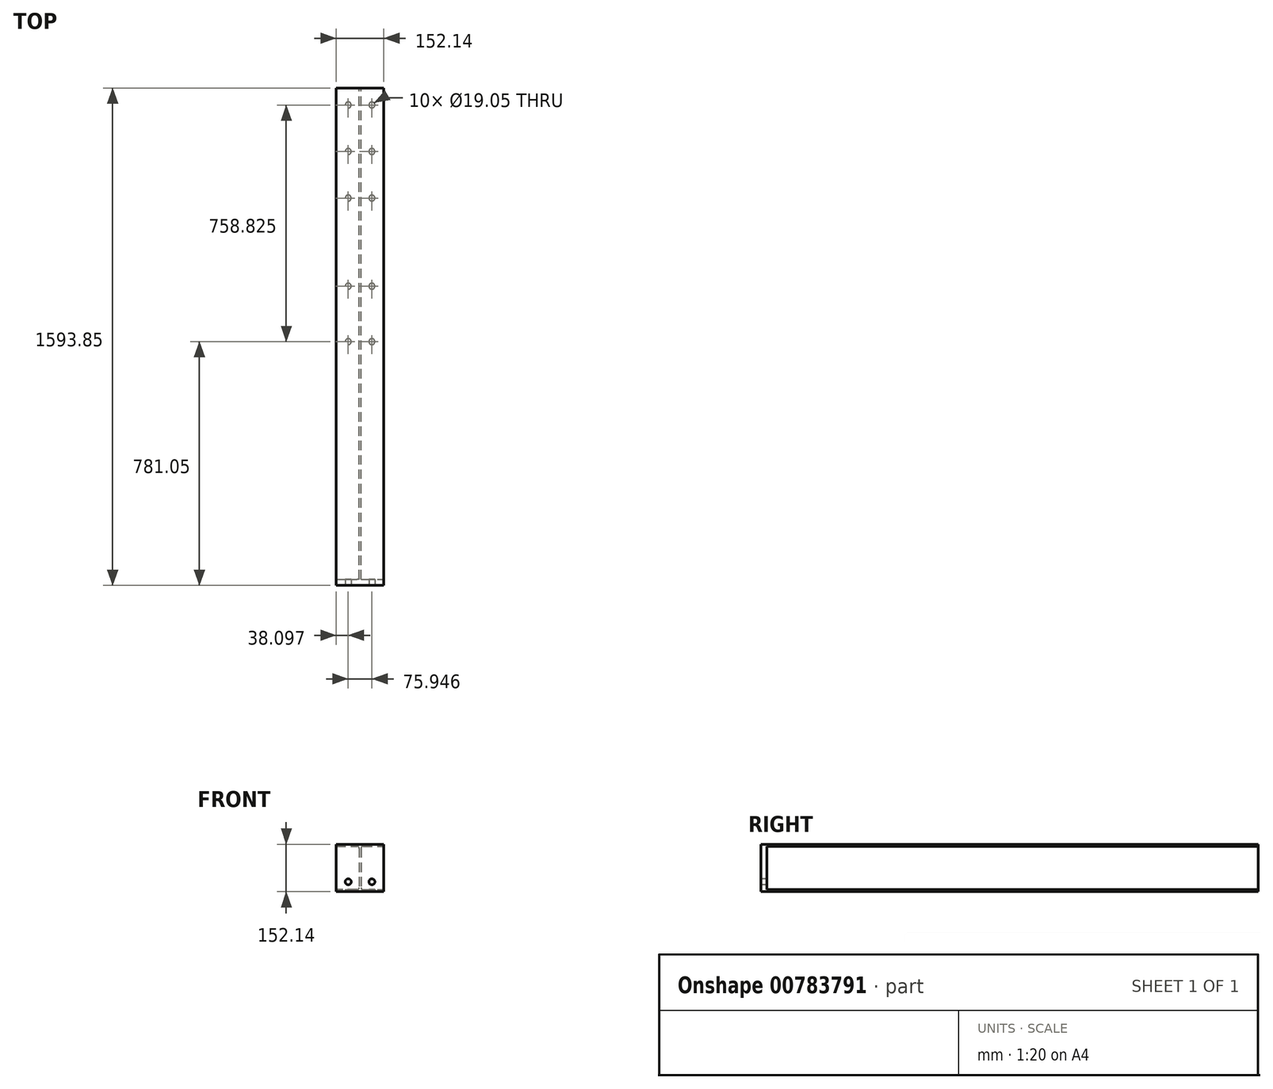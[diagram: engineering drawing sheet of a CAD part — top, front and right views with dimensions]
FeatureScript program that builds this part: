
annotation { "Feature Type Name" : "Feature", "Feature Type Description" : "" }
export const myFeature = defineFeature(function(context is Context, id is Id, definition is map)
    precondition{}
    {
        {
            var Q0;
            Q0=qCreatedBy(makeId("Front.planeOp"),FACE);
            var sketch = newSketch(context, id + "F0", { "sketchPlane" : qUnion([Q0])});
            skLineSegment(sketch, "E0", {"start": v(0, -76.07) * mm, "end": v(0, 76.07) * mm, "construction": true});
            skLineSegment(sketch, "E1", {"start": v(-76.07, 76.07) * mm, "end": v(76.07, 76.07) * mm});
            skLineSegment(sketch, "E2", {"start": v(-76.07, -76.07) * mm, "end": v(76.07, -76.07) * mm});
            skLineSegment(sketch, "E3", {"start": v(-76.07, 76.07) * mm, "end": v(-76.07, 69.47) * mm});
            skLineSegment(sketch, "E4", {"start": v(-76.07, 69.47) * mm, "end": v(-9.27, 69.47) * mm});
            skLineSegment(sketch, "E5", {"start": v(-2.92, 63.12) * mm, "end": v(-2.92, -63.12) * mm});
            skLineSegment(sketch, "E6", {"start": v(-9.27, -69.47) * mm, "end": v(-76.07, -69.47) * mm});
            skLineSegment(sketch, "E7", {"start": v(-76.07, -69.47) * mm, "end": v(-76.07, -76.07) * mm});
            skLineSegment(sketch, "E8", {"start": v(-2.92, 69.47) * mm, "end": v(2.92, 69.47) * mm, "construction": true});
            skLineSegment(sketch, "E9", {"start": v(9.27, 69.47) * mm, "end": v(76.07, 69.47) * mm});
            skLineSegment(sketch, "E10", {"start": v(76.07, 69.47) * mm, "end": v(76.07, 76.07) * mm});
            skLineSegment(sketch, "E11", {"start": v(-2.92, -69.47) * mm, "end": v(2.92, -69.47) * mm, "construction": true});
            skLineSegment(sketch, "E12", {"start": v(2.92, 63.12) * mm, "end": v(2.92, -63.12) * mm});
            skLineSegment(sketch, "E13", {"start": v(9.27, -69.47) * mm, "end": v(76.07, -69.47) * mm});
            skLineSegment(sketch, "E14", {"start": v(76.07, -69.47) * mm, "end": v(76.07, -76.07) * mm});
            skLineSegment(sketch, "E15", {"start": v(0, 69.47) * mm, "end": v(0, -69.47) * mm, "construction": true});
            skPoint(sketch, "E16.visualSharp", {"position": v(2.92, 69.47) * mm});
            skArc(sketch, "E16.filletArc", {"start": v(9.27, 69.47) * mm, "mid": v(4.78, 67.6) * mm, "end": v(2.92, 63.12) * mm});
            skPoint(sketch, "E17.visualSharp", {"position": v(-2.92, 69.47) * mm});
            skArc(sketch, "E17.filletArc", {"start": v(-2.92, 63.12) * mm, "mid": v(-4.78, 67.6) * mm, "end": v(-9.27, 69.47) * mm});
            skPoint(sketch, "E18.visualSharp", {"position": v(-2.92, -69.47) * mm});
            skArc(sketch, "E18.filletArc", {"start": v(-9.27, -69.47) * mm, "mid": v(-4.78, -67.6) * mm, "end": v(-2.92, -63.12) * mm});
            skPoint(sketch, "E19.visualSharp", {"position": v(2.92, -69.47) * mm});
            skArc(sketch, "E19.filletArc", {"start": v(2.92, -63.12) * mm, "mid": v(4.78, -67.6) * mm, "end": v(9.27, -69.47) * mm});
            skSolve(sketch);
        }
        {
            var Q0;
            Q0=makeQuery(id+"F0.imprint","IMPRINT",FACE,{"disambiguationData":[TD([[makeQuery(id+"F0.imprint","IMPRINT",EDGE,{"derivedFrom":sQuery(id+"F0.wireOp",EDGE,"E1")}),-1.0]])]});
            extrude(context, id + "F1", {"entities" : qUnion([Q0]), "depth" : 1574.8 * mm, "offsetDistance" : 25.4 * mm});
        }
        {
            var Q0;
            Q0=makeQuery(id+"F1.opExtrude","CAP_FACE",FACE,{"disambiguationData":[OSD([sQuery(id+"F0.wireOp",EDGE,"E1"),sQuery(id+"F0.wireOp",EDGE,"E2"),sQuery(id+"F0.wireOp",EDGE,"E3"),sQuery(id+"F0.wireOp",EDGE,"E4"),sQuery(id+"F0.wireOp",EDGE,"E5"),sQuery(id+"F0.wireOp",EDGE,"E6"),sQuery(id+"F0.wireOp",EDGE,"E7"),sQuery(id+"F0.wireOp",EDGE,"E9"),sQuery(id+"F0.wireOp",EDGE,"E10"),sQuery(id+"F0.wireOp",EDGE,"E12"),sQuery(id+"F0.wireOp",EDGE,"E13"),sQuery(id+"F0.wireOp",EDGE,"E14"),sQuery(id+"F0.wireOp",EDGE,"E16.filletArc"),sQuery(id+"F0.wireOp",EDGE,"E17.filletArc"),sQuery(id+"F0.wireOp",EDGE,"E18.filletArc"),sQuery(id+"F0.wireOp",EDGE,"E19.filletArc")])],"isStart":false});
            var sketch = newSketch(context, id + "F2", { "sketchPlane" : qUnion([Q0])});
            skLineSegment(sketch, "E20.0", {"start": v(-76.07, 76.07) * mm, "end": v(76.07, 76.07) * mm});
            skLineSegment(sketch, "E20.1", {"start": v(-76.07, -76.07) * mm, "end": v(76.07, -76.07) * mm});
            skLineSegment(sketch, "E21", {"start": v(-76.07, 76.07) * mm, "end": v(-76.07, -76.07) * mm});
            skLineSegment(sketch, "E22", {"start": v(76.07, -76.07) * mm, "end": v(76.07, 76.07) * mm});
            skSolve(sketch);
        }
        {
            var Q0;
            {var subQ1=makeQuery(id+"F1.opExtrude","CAP_EDGE",EDGE,{"disambiguationData":[OSD([sQuery(id+"F0.wireOp",EDGE,"E4")])],"isStart":false});Q0=makeQuery(id+"F2.imprint","IMPRINT",FACE,{"disambiguationData":[TD([[makeQuery(id+"F2.imprint","IMPRINT",EDGE,{"derivedFrom":subQ1}),-1.0]])]});}
            var Q1;
            {var subQ3=sQuery(id+"F2.wireOp",EDGE,"E20.0");Q1=makeQuery(id+"F2.imprint","IMPRINT",FACE,{"disambiguationData":[TD([[makeQuery(id+"F2.imprint","IMPRINT",EDGE,{"derivedFrom":subQ3}),-1.0]])]});}
            var Q2;
            {var subQ1=makeQuery(id+"F1.opExtrude","CAP_EDGE",EDGE,{"disambiguationData":[OSD([sQuery(id+"F0.wireOp",EDGE,"E9")])],"isStart":false});Q2=makeQuery(id+"F2.imprint","IMPRINT",FACE,{"disambiguationData":[TD([[makeQuery(id+"F2.imprint","IMPRINT",EDGE,{"derivedFrom":subQ1}),-1.0]])]});}
            extrude(context, id + "F3", {"entities" : qUnion([Q0, Q1, Q2]), "operationType" : NewBodyOperationType.ADD, "depth" : 19.05 * mm, "offsetDistance" : 25.4 * mm});
        }
        {
            var Q0;
            Q0=makeQuery(id+"F3.opExtrude","CAP_FACE",FACE,{"disambiguationData":[OSD([sQuery(id+"F2.wireOp",EDGE,"E20.0"),sQuery(id+"F2.wireOp",EDGE,"E20.1"),sQuery(id+"F2.wireOp",EDGE,"E21"),sQuery(id+"F2.wireOp",EDGE,"E22")])],"isStart":false});
            var sketch = newSketch(context, id + "F4", { "sketchPlane" : qUnion([Q0])});
            skLineSegment(sketch, "E23", {"start": v(-37.97, 76.07) * mm, "end": v(-37.97, -76.07) * mm, "construction": true});
            skLineSegment(sketch, "E24", {"start": v(37.97, 76.07) * mm, "end": v(37.97, -76.07) * mm, "construction": true});
            skLineSegment(sketch, "E25", {"start": v(-37.97, -44.32) * mm, "end": v(37.97, -44.32) * mm, "construction": true});
            skCircle(sketch, "E26", {"center": v(-37.97, -44.32) * mm, "radius": 9.53 * mm});
            skCircle(sketch, "E27", {"center": v(37.97, -44.32) * mm, "radius": 9.53 * mm});
            skSolve(sketch);
        }
        {
            var Q0;
            Q0=makeQuery(id+"F4.imprint","IMPRINT",FACE,{"disambiguationData":[TD([[makeQuery(id+"F4.imprint","IMPRINT",EDGE,{"derivedFrom":sQuery(id+"F4.wireOp",EDGE,"E26")}),1.0]])]});
            var Q1;
            Q1=makeQuery(id+"F4.imprint","IMPRINT",FACE,{"disambiguationData":[TD([[makeQuery(id+"F4.imprint","IMPRINT",EDGE,{"derivedFrom":sQuery(id+"F4.wireOp",EDGE,"E27")}),1.0]])]});
            extrude(context, id + "F5", {"entities" : qUnion([Q0, Q1]), "operationType" : NewBodyOperationType.REMOVE, "oppositeDirection" : true, "depth" : 43.94 * mm, "offsetDistance" : 25.4 * mm});
        }
        {
            var Q0;
            Q0=makeQuery(id+"F3.boolean.opBoolean","MERGE",FACE,{"derivedFrom":[makeQuery(id+"F1.opExtrude","SWEPT_FACE",FACE,{"disambiguationData":[OSD([sQuery(id+"F0.wireOp",EDGE,"E2")])]}),makeQuery(id+"F3.opExtrude","SWEPT_FACE",FACE,{"disambiguationData":[OSD([sQuery(id+"F2.wireOp",EDGE,"E20.1")])]})]});
            var sketch = newSketch(context, id + "F6", { "sketchPlane" : qUnion([Q0])});
            skLineSegment(sketch, "E28", {"start": v(76.07, 53.98) * mm, "end": v(-76.07, 53.97) * mm, "construction": true});
            skLineSegment(sketch, "E29", {"start": v(76.07, 203.2) * mm, "end": v(-76.07, 203.2) * mm, "construction": true});
            skLineSegment(sketch, "E30", {"start": v(76.07, 352.43) * mm, "end": v(-76.07, 352.43) * mm, "construction": true});
            skLineSegment(sketch, "E31", {"start": v(76.07, 635) * mm, "end": v(-76.07, 635) * mm, "construction": true});
            skLineSegment(sketch, "E32.0", {"start": v(-9.27, 1574.8) * mm, "end": v(-76.07, 1574.8) * mm, "construction": true});
            skLineSegment(sketch, "E33", {"start": v(-76.07, 812.8) * mm, "end": v(76.07, 812.8) * mm, "construction": true});
            skLineSegment(sketch, "E34", {"start": v(-37.97, 0) * mm, "end": v(-37.97, 812.8) * mm, "construction": true});
            skLineSegment(sketch, "E35", {"start": v(37.97, 0) * mm, "end": v(37.97, 812.8) * mm, "construction": true});
            skCircle(sketch, "E36", {"center": v(-37.97, 53.97) * mm, "radius": 9.53 * mm});
            skCircle(sketch, "E37", {"center": v(37.97, 53.97) * mm, "radius": 9.53 * mm});
            skCircle(sketch, "E38", {"center": v(37.97, 203.2) * mm, "radius": 9.53 * mm});
            skCircle(sketch, "E39", {"center": v(-37.97, 203.2) * mm, "radius": 9.53 * mm});
            skCircle(sketch, "E40", {"center": v(-37.97, 352.43) * mm, "radius": 9.53 * mm});
            skCircle(sketch, "E41", {"center": v(37.97, 352.43) * mm, "radius": 9.53 * mm});
            skCircle(sketch, "E42", {"center": v(37.97, 635) * mm, "radius": 9.53 * mm});
            skCircle(sketch, "E43", {"center": v(-37.97, 635) * mm, "radius": 9.53 * mm});
            skCircle(sketch, "E44", {"center": v(-37.97, 812.8) * mm, "radius": 9.53 * mm});
            skCircle(sketch, "E45", {"center": v(37.97, 812.8) * mm, "radius": 9.53 * mm});
            skSolve(sketch);
        }
        {
            var Q0;
            Q0=makeQuery(id+"F6.imprint","IMPRINT",FACE,{"disambiguationData":[TD([[makeQuery(id+"F6.imprint","IMPRINT",EDGE,{"derivedFrom":sQuery(id+"F6.wireOp",EDGE,"E44")}),1.0]])]});
            var Q1;
            Q1=makeQuery(id+"F6.imprint","IMPRINT",FACE,{"disambiguationData":[TD([[makeQuery(id+"F6.imprint","IMPRINT",EDGE,{"derivedFrom":sQuery(id+"F6.wireOp",EDGE,"E45")}),1.0]])]});
            var Q2;
            Q2=makeQuery(id+"F6.imprint","IMPRINT",FACE,{"disambiguationData":[TD([[makeQuery(id+"F6.imprint","IMPRINT",EDGE,{"derivedFrom":sQuery(id+"F6.wireOp",EDGE,"E43")}),1.0]])]});
            var Q3;
            Q3=makeQuery(id+"F6.imprint","IMPRINT",FACE,{"disambiguationData":[TD([[makeQuery(id+"F6.imprint","IMPRINT",EDGE,{"derivedFrom":sQuery(id+"F6.wireOp",EDGE,"E42")}),1.0]])]});
            var Q4;
            Q4=makeQuery(id+"F6.imprint","IMPRINT",FACE,{"disambiguationData":[TD([[makeQuery(id+"F6.imprint","IMPRINT",EDGE,{"derivedFrom":sQuery(id+"F6.wireOp",EDGE,"E40")}),1.0]])]});
            var Q5;
            Q5=makeQuery(id+"F6.imprint","IMPRINT",FACE,{"disambiguationData":[TD([[makeQuery(id+"F6.imprint","IMPRINT",EDGE,{"derivedFrom":sQuery(id+"F6.wireOp",EDGE,"E41")}),1.0]])]});
            var Q6;
            Q6=makeQuery(id+"F6.imprint","IMPRINT",FACE,{"disambiguationData":[TD([[makeQuery(id+"F6.imprint","IMPRINT",EDGE,{"derivedFrom":sQuery(id+"F6.wireOp",EDGE,"E39")}),1.0]])]});
            var Q7;
            Q7=makeQuery(id+"F6.imprint","IMPRINT",FACE,{"disambiguationData":[TD([[makeQuery(id+"F6.imprint","IMPRINT",EDGE,{"derivedFrom":sQuery(id+"F6.wireOp",EDGE,"E38")}),1.0]])]});
            var Q8;
            Q8=makeQuery(id+"F6.imprint","IMPRINT",FACE,{"disambiguationData":[TD([[makeQuery(id+"F6.imprint","IMPRINT",EDGE,{"derivedFrom":sQuery(id+"F6.wireOp",EDGE,"E36")}),1.0]])]});
            var Q9;
            Q9=makeQuery(id+"F6.imprint","IMPRINT",FACE,{"disambiguationData":[TD([[makeQuery(id+"F6.imprint","IMPRINT",EDGE,{"derivedFrom":sQuery(id+"F6.wireOp",EDGE,"E37")}),1.0]])]});
            extrude(context, id + "F7", {"entities" : qUnion([Q0, Q1, Q2, Q3, Q4, Q5, Q6, Q7, Q8, Q9]), "operationType" : NewBodyOperationType.REMOVE, "oppositeDirection" : true, "depth" : 25.4 * mm, "offsetDistance" : 25.4 * mm});
        }
    });
